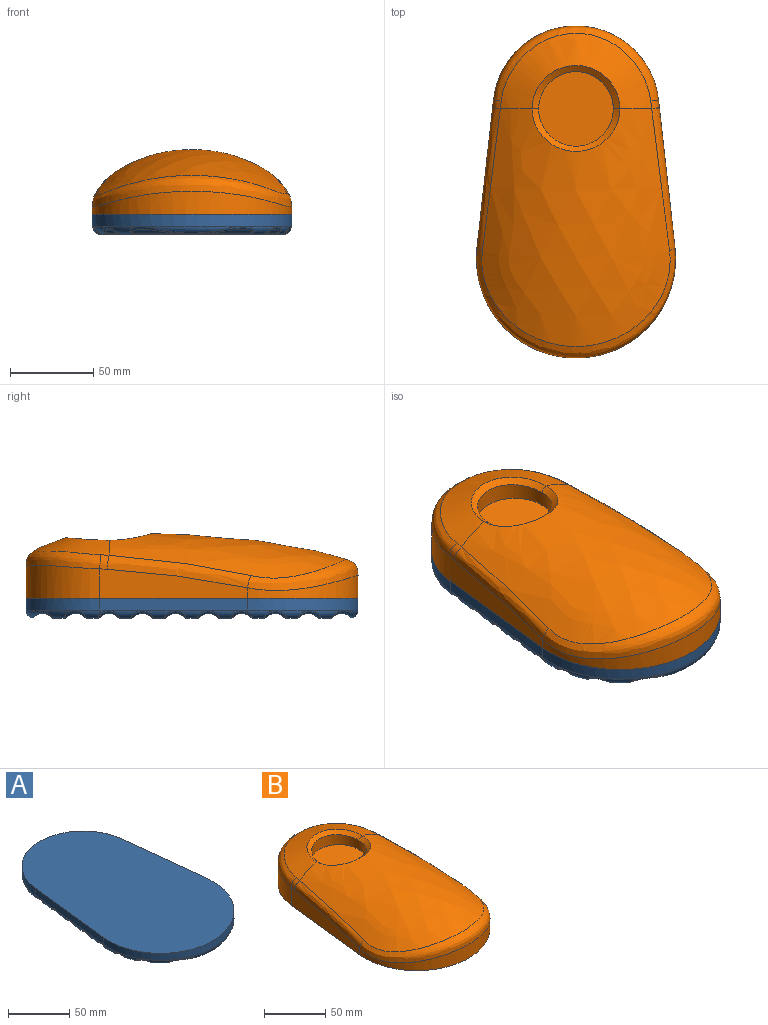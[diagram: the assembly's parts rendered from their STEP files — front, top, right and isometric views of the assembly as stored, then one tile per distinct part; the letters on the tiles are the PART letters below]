
ASSEMBLY  parts=2 mates=1
PART A: 88 faces, bbox 121.2x209.1x12.1 mm
  f0: torus R=45mm, axis (0,0,1), area 97.3mm2, adj f32,f35,f83,f86
  f1: torus R=45mm, axis (0,0,1), area 71.2mm2, adj f25,f30,f35,f81,f84
  f2: torus R=45mm, axis (0,0,1), area 97.3mm2, adj f32,f35,f84,f86
  f3: torus R=45mm, axis (0,0,1), area 163.8mm2, adj f35,f86
  f4: cylinder r=5mm len=20.56mm, axis (-0.11,-0.99,0), area 72.5mm2, adj f24,f36,f60,f64
  f5: cylinder r=5mm len=20.56mm, axis (-0.11,-0.99,0), area 72.5mm2, adj f27,f36,f64,f68
  f6: cylinder r=5mm len=20.56mm, axis (-0.11,-0.99,0), area 72.5mm2, adj f28,f36,f68,f72
  f7: cylinder r=5mm len=20.56mm, axis (-0.11,-0.99,0), area 72.5mm2, adj f29,f36,f72,f76
  f8: cylinder r=5mm len=5.42mm, axis (-0.11,-0.99,0), area 4.8mm2, adj f31,f36,f76
  f9: cylinder r=5mm len=3.57mm, axis (-0.11,0.99,0), area 1.4mm2, adj f21,f37,f63
  f10: cylinder r=5mm len=20.56mm, axis (-0.11,0.99,0), area 72.5mm2, adj f24,f37,f63,f67
  f11: cylinder r=5mm len=20.56mm, axis (-0.11,0.99,0), area 72.5mm2, adj f27,f37,f67,f71
  f12: cylinder r=5mm len=20.56mm, axis (-0.11,0.99,0), area 72.5mm2, adj f28,f37,f71,f75
  f13: cylinder r=5mm len=20.56mm, axis (-0.11,0.99,0), area 72.5mm2, adj f29,f37,f75,f79
  f14: torus R=55mm, axis (0,0,1), area 104.6mm2, adj f20,f34,f48,f51
  f15: torus R=55mm, axis (0,0,1), area 178.8mm2, adj f34,f48
  f16: torus R=55mm, axis (0,0,1), area 79mm2, adj f22,f34,f51,f55
  f17: torus R=55mm, axis (0,0,1), area 104.6mm2, adj f20,f34,f48,f52
  f18: torus R=55mm, axis (0,0,1), area 72.5mm2, adj f23,f26,f34,f55,f58
  f19: torus R=55mm, axis (0,0,1), area 79mm2, adj f22,f34,f52,f56
  f20: plane 81.52x6.14mm, normal (0,0,-1), area 462.7mm2, adj f14,f17,f49,f50
  f21: torus R=55mm, axis (0,0,1), area 72.5mm2, adj f9,f23,f34,f56,f61
  f22: plane 104.66x6.14mm, normal (0,0,-1), area 629.1mm2, adj f16,f19,f53,f54
  f23: plane 110x6.14mm, normal (0,0,-1), area 675.4mm2, adj f18,f21,f57,f59
  f24: plane 106.9x6.14mm, normal (0,0,-1), area 652.5mm2, adj f4,f10,f62,f65
  f25: cylinder r=5mm len=5.42mm, axis (-0.11,0.99,0), area 4.8mm2, adj f1,f37,f79
  f26: cylinder r=5mm len=3.57mm, axis (-0.11,-0.99,0), area 1.4mm2, adj f18,f36,f60
  f27: plane 102.43x6.14mm, normal (0,0,-1), area 625.1mm2, adj f5,f11,f66,f69
  f28: plane 97.96x6.14mm, normal (0,0,-1), area 597.6mm2, adj f6,f12,f70,f73
  f29: plane 93.48x6.14mm, normal (0,0,-1), area 570.1mm2, adj f7,f13,f74,f77
  f30: plane 88.93x6.14mm, normal (0,0,-1), area 538.6mm2, adj f1,f31,f80,f82
  f31: torus R=45mm, axis (0,0,1), area 71.2mm2, adj f8,f30,f35,f78,f83
  f32: plane 72.11x6.14mm, normal (0,0,-1), area 411.1mm2, adj f0,f2,f85,f87
  f33: plane 200x120mm, normal (0,0,1), area 19543mm2, adj f34,f35,f36,f37
  f34: cylinder r=60mm len=120mm, axis (0,0,-1), area 1413mm2, adj f14,f15,f16,f17,f18,f19,f21,f33
  f35: cylinder r=50mm len=99.38mm, axis (0,0,-1), area 1021.6mm2, adj f0,f1,f2,f3,f31,f33,f36,f37
  f36: plane 88.89x9.94mm, normal (-0.99,0.11,0), area 626.1mm2, adj f4,f5,f6,f7,f8,f26,f33,f34
  f37: plane 88.89x9.94mm, normal (0.99,0.11,0), area 626.1mm2, adj f9,f10,f11,f12,f13,f25,f33,f34
  f38: cylinder r=7.5mm len=65.24mm, axis (-1,0,0), area 589.9mm2, adj f86,f87
  f39: cylinder r=7.5mm len=90.44mm, axis (-1,0,0), area 1053.1mm2, adj f82,f83,f84,f85
  f40: cylinder r=7.5mm len=97.23mm, axis (-1,0,0), area 1174.5mm2, adj f76,f77,f78,f79,f80,f81
  f41: cylinder r=7.5mm len=101.71mm, axis (-1,0,0), area 1229.4mm2, adj f72,f73,f74,f75
  f42: cylinder r=7.5mm len=106.18mm, axis (-1,0,0), area 1284.2mm2, adj f68,f69,f70,f71
  f43: cylinder r=7.5mm len=110.65mm, axis (-1,0,0), area 1339mm2, adj f64,f65,f66,f67
  f44: cylinder r=7.5mm len=115.12mm, axis (-1,0,0), area 1393.6mm2, adj f58,f59,f60,f61,f62,f63
  f45: cylinder r=7.5mm len=115.12mm, axis (-1,0,0), area 1387mm2, adj f54,f55,f56,f57
  f46: cylinder r=7.5mm len=103.91mm, axis (-1,0,0), area 1199.6mm2, adj f50,f51,f52,f53
  f47: cylinder r=7.5mm len=72.82mm, axis (-1,0,0), area 654.8mm2, adj f48,f49
  f48: bspline ~74.72x14.7mm, area 241.6mm2, adj f14,f15,f17,f47,f49
  f49: cylinder r=2mm len=68.41mm, axis (-1,0,0), area 111.8mm2, adj f20,f47,f48
  f50: cylinder r=2mm len=81.52mm, axis (-1,0,0), area 133.2mm2, adj f20,f46,f51,f52
  f51: bspline ~14.22x13.53mm, area 55.6mm2, adj f14,f16,f46,f50,f53
  f52: bspline ~14.26x13.62mm, area 55.6mm2, adj f17,f19,f46,f50,f53
  f53: cylinder r=2mm len=99.85mm, axis (-1,0,0), area 163.2mm2, adj f22,f46,f51,f52
  f54: cylinder r=2mm len=104.66mm, axis (-1,0,0), area 171.1mm2, adj f22,f45,f55,f56
  f55: bspline ~13.93x7.91mm, area 48mm2, adj f16,f18,f45,f54,f57
  f56: bspline ~13.93x7.92mm, area 48mm2, adj f19,f21,f45,f54,f57
  f57: cylinder r=2mm len=109.83mm, axis (-1,0,0), area 179.5mm2, adj f23,f45,f55,f56
  f58: bspline ~4.93x4.82mm, area 12.3mm2, adj f18,f44,f59,f60
  f59: cylinder r=2mm len=109.83mm, axis (-1,0,0), area 179.5mm2, adj f23,f44,f58,f61
  f60: bspline ~10.45x6.88mm, area 33.2mm2, adj f4,f26,f44,f58,f62
  f61: bspline ~4.93x4.82mm, area 12.3mm2, adj f21,f44,f59,f63
  f62: cylinder r=2mm len=106.9mm, axis (-1,0,0), area 174.7mm2, adj f24,f44,f60,f63
  f63: bspline ~10.65x6.87mm, area 33.2mm2, adj f9,f10,f44,f61,f62
  f64: bspline ~13.88x6.76mm, area 45.1mm2, adj f4,f5,f43,f65,f66
  f65: cylinder r=2mm len=105.53mm, axis (-1,0,0), area 172.5mm2, adj f24,f43,f64,f67
  f66: cylinder r=2mm len=102.43mm, axis (-1,0,0), area 167.4mm2, adj f27,f43,f64,f67
  f67: bspline ~13.88x6.87mm, area 45.1mm2, adj f10,f11,f43,f65,f66
  f68: bspline ~13.88x6.76mm, area 45.1mm2, adj f5,f6,f42,f69,f70
  f69: cylinder r=2mm len=101.05mm, axis (-1,0,0), area 165.2mm2, adj f27,f42,f68,f71
  f70: cylinder r=2mm len=97.96mm, axis (-1,0,0), area 160.1mm2, adj f28,f42,f68,f71
  f71: bspline ~13.88x6.87mm, area 45.1mm2, adj f11,f12,f42,f69,f70
  f72: bspline ~13.88x6.76mm, area 45.1mm2, adj f6,f7,f41,f73,f74
  f73: cylinder r=2mm len=96.58mm, axis (-1,0,0), area 157.9mm2, adj f28,f41,f72,f75
  f74: cylinder r=2mm len=93.48mm, axis (-1,0,0), area 152.8mm2, adj f29,f41,f72,f75
  f75: bspline ~13.88x6.87mm, area 45.1mm2, adj f12,f13,f41,f73,f74
  f76: bspline ~12.77x5.43mm, area 36.7mm2, adj f7,f8,f40,f77,f78
  f77: cylinder r=2mm len=92.11mm, axis (-1,0,0), area 150.6mm2, adj f29,f40,f76,f79
  f78: bspline ~5.62x3.19mm, area 8.6mm2, adj f31,f40,f76,f80
  f79: bspline ~12.77x5.41mm, area 36.7mm2, adj f13,f25,f40,f77,f81
  f80: cylinder r=2mm len=88.93mm, axis (-1,0,0), area 145.4mm2, adj f30,f40,f78,f81
  f81: bspline ~5.62x3.19mm, area 8.6mm2, adj f1,f40,f79,f80
  f82: cylinder r=2mm len=86.12mm, axis (-1,0,0), area 140.8mm2, adj f30,f39,f83,f84
  f83: bspline ~14.15x11.43mm, area 52.9mm2, adj f0,f31,f39,f82,f85
  f84: bspline ~14.15x11.07mm, area 52.9mm2, adj f1,f2,f39,f82,f85
  f85: cylinder r=2mm len=72.11mm, axis (-1,0,0), area 117.9mm2, adj f32,f39,f83,f84
  f86: bspline ~67.35x14.66mm, area 222.2mm2, adj f0,f2,f3,f38,f87
  f87: cylinder r=2mm len=61.03mm, axis (-1,0,0), area 99.8mm2, adj f32,f38,f86
PART B: 17 faces, bbox 152.1x230.8x87.3 mm
  f0: bspline ~163.3x150mm, area 13979.3mm2, adj f1,f8,f10,f12,f16
  f1: bspline ~150x72.18mm, area 2328.8mm2, adj f0,f9,f11,f13,f15
  f2: plane 90.99x19.89mm, normal (0.99,0.11,0), area 1184mm2, adj f4,f5,f12,f13,f14
  f3: plane 90.99x19.89mm, normal (-0.99,0.11,0), area 1184mm2, adj f4,f5,f8,f9,f14
  f4: cylinder r=50mm len=99.38mm, axis (0,0,-1), area 2596.5mm2, adj f2,f3,f11,f14
  f5: cylinder r=60mm len=120mm, axis (0,0,-1), area 1792.2mm2, adj f2,f3,f10,f14
  f6: cylinder r=22.5mm len=45mm, axis (0,0,-1), area 1300mm2, adj f7,f15,f16
  f7: plane 45x45mm, normal (0,0,1), area 1590.4mm2, adj f6
  f8: bspline ~86.46x19.58mm, area 822.8mm2, adj f0,f3,f9,f10
  f9: bspline ~8.72x5.56mm, area 47.8mm2, adj f1,f3,f8,f11
  f10: bspline ~120.25x66.67mm, area 2099mm2, adj f0,f5,f8,f12
  f11: bspline ~99.43x45.29mm, area 1490.8mm2, adj f1,f4,f9,f13
  f12: bspline ~86.46x19.58mm, area 822.8mm2, adj f0,f2,f10,f13
  f13: bspline ~8.72x5.56mm, area 47.8mm2, adj f1,f2,f11,f12
  f14: plane 200x120mm, normal (0,0,-1), area 19543mm2, adj f2,f3,f4,f5
  f15: bspline ~52.87x26.21mm, area 366.2mm2, adj f1,f6,f16
  f16: bspline ~52.87x25.57mm, area 350.7mm2, adj f0,f6,f15
PLACE A t=(-262.57,201.44,-8.11)mm
PLACE B t=(-262.57,201.44,-8.11)mm
MATE fastened A.f33 <-> B.f14  axis (0,0,1) through (-362.57,148.67,3.89)mm
